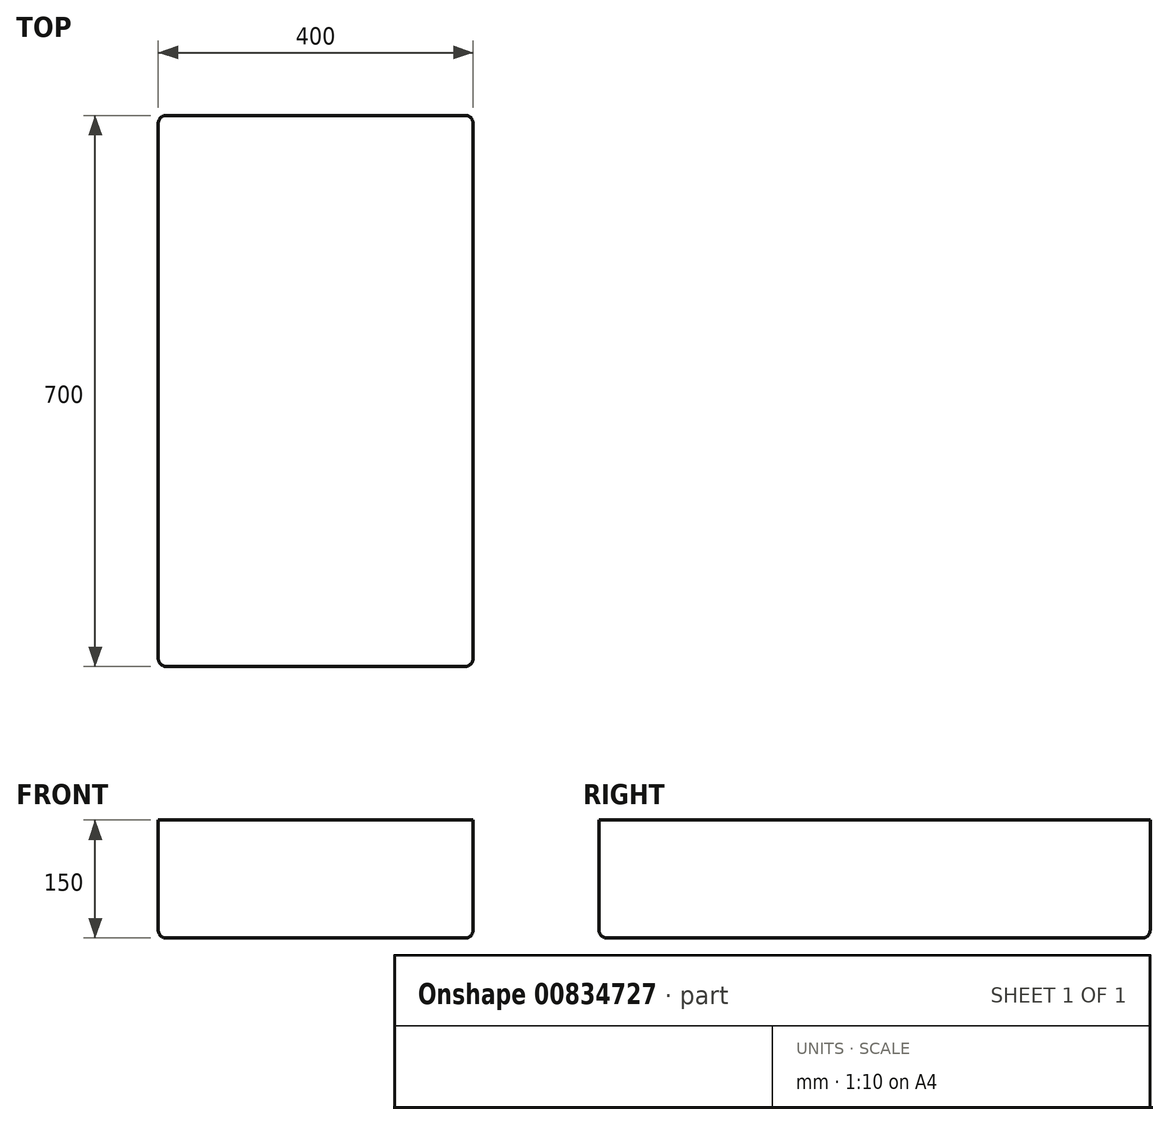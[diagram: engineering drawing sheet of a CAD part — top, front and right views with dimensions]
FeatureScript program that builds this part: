
annotation { "Feature Type Name" : "Feature", "Feature Type Description" : "" }
export const myFeature = defineFeature(function(context is Context, id is Id, definition is map)
    precondition{}
    {
        {
            var Q0;
            Q0=qCreatedBy(makeId("Top.planeOp"),FACE);
            var sketch = newSketch(context, id + "F0", { "sketchPlane" : qUnion([Q0])});
            skLineSegment(sketch, "E0.bottom", {"start": v(200, 350) * mm, "end": v(-200, 350) * mm});
            skLineSegment(sketch, "E0.top", {"start": v(200, -350) * mm, "end": v(-200, -350) * mm});
            skLineSegment(sketch, "E0.left", {"start": v(200, 350) * mm, "end": v(200, -350) * mm});
            skLineSegment(sketch, "E0.right", {"start": v(-200, 350) * mm, "end": v(-200, -350) * mm});
            skPoint(sketch, "E0.middle", {"position": v(0, 0) * mm});
            skSolve(sketch);
        }
        {
            var Q0;
            Q0=makeQuery(id+"F0.imprint","IMPRINT",FACE,{"disambiguationData":[TD([[makeQuery(id+"F0.imprint","IMPRINT",EDGE,{"derivedFrom":sQuery(id+"F0.wireOp",EDGE,"E0.bottom")}),1.0]])]});
            extrude(context, id + "F1", {"entities" : qUnion([Q0]), "depth" : 150 * mm, "offsetDistance" : 25 * mm});
        }
        {
            var Q0;
            Q0=makeQuery(id+"F1.opExtrude","SWEPT_EDGE",EDGE,{"disambiguationData":[OSD([sQuery(id+"F0.wireOp",EDGE,"E0.bottom"),sQuery(id+"F0.wireOp",EDGE,"E0.left")])]});
            var Q1;
            Q1=makeQuery(id+"F1.opExtrude","SWEPT_EDGE",EDGE,{"disambiguationData":[OSD([sQuery(id+"F0.wireOp",EDGE,"E0.top"),sQuery(id+"F0.wireOp",EDGE,"E0.left")])]});
            var Q2;
            Q2=makeQuery(id+"F1.opExtrude","SWEPT_EDGE",EDGE,{"disambiguationData":[OSD([sQuery(id+"F0.wireOp",EDGE,"E0.top"),sQuery(id+"F0.wireOp",EDGE,"E0.right")])]});
            var Q3;
            Q3=makeQuery(id+"F1.opExtrude","SWEPT_EDGE",EDGE,{"disambiguationData":[OSD([sQuery(id+"F0.wireOp",EDGE,"E0.bottom"),sQuery(id+"F0.wireOp",EDGE,"E0.right")])]});
            fillet(context, id + "F2", {"entities" : qUnion([Q0, Q1, Q2, Q3]), "radius" : 10 * mm, "tangentPropagation" : true, "allowEdgeOverflow" : false});
        }
        {
            var Q0;
            Q0=makeQuery(id+"F1.opExtrude","CAP_EDGE",EDGE,{"disambiguationData":[OSD([sQuery(id+"F0.wireOp",EDGE,"E0.left")])],"isStart":true});
            var Q1;
            Q1=makeQuery(id+"F1.opExtrude","CAP_EDGE",EDGE,{"disambiguationData":[OSD([sQuery(id+"F0.wireOp",EDGE,"E0.bottom")])],"isStart":true});
            var Q2;
            Q2=makeQuery(id+"F1.opExtrude","CAP_EDGE",EDGE,{"disambiguationData":[OSD([sQuery(id+"F0.wireOp",EDGE,"E0.right")])],"isStart":true});
            fillet(context, id + "F3", {"entities" : qUnion([Q0, Q1, Q2]), "radius" : 10 * mm, "tangentPropagation" : true, "allowEdgeOverflow" : false});
        }
    });
